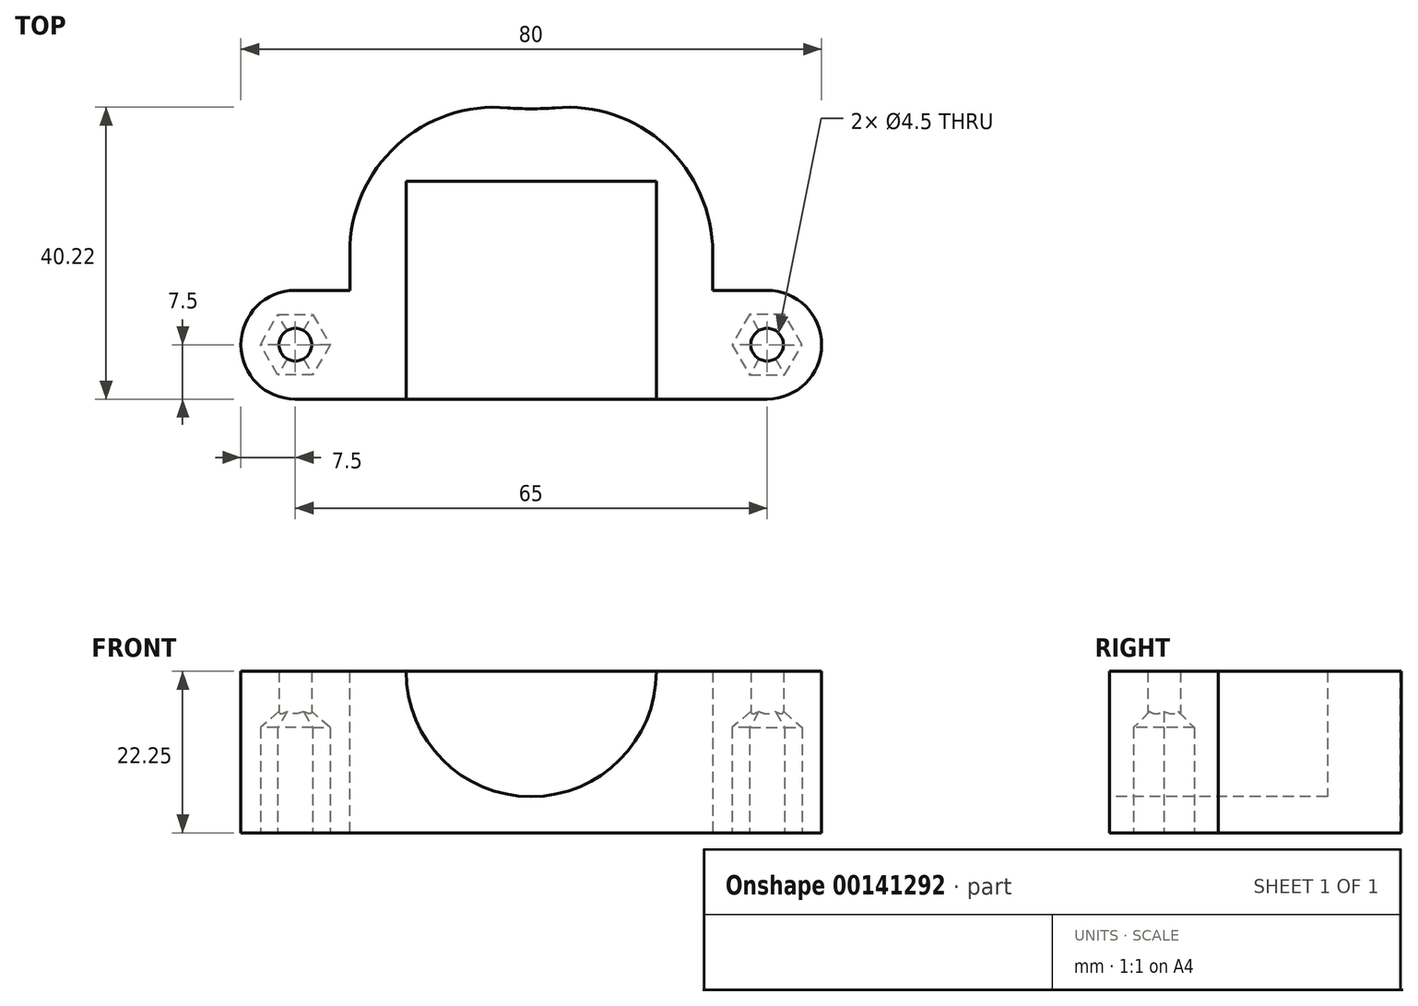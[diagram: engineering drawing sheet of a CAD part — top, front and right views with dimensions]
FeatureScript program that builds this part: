
annotation { "Feature Type Name" : "Feature", "Feature Type Description" : "" }
export const myFeature = defineFeature(function(context is Context, id is Id, definition is map)
    precondition{}
    {
        {
            var Q0;
            Q0=qCreatedBy(makeId("Top.planeOp"),FACE);
            var sketch = newSketch(context, id + "F0", { "sketchPlane" : qUnion([Q0])});
            skArc(sketch, "E0", {"start": v(38.1, 0) * mm, "mid": v(0, 38.1) * mm, "end": v(-38.1, 0) * mm});
            skCircle(sketch, "E1", {"center": v(0, 0) * mm, "radius": 5 * mm});
            skArc(sketch, "E2", {"start": v(-38.1, 0) * mm, "mid": v(0, -38.1) * mm, "end": v(38.1, 0) * mm});
            skSolve(sketch);
        }
        {
            var Q0;
            Q0=qSketchRegion(id+"F0",true);
            extrude(context, id + "F1", {"entities" : qUnion([Q0]), "depth" : 14 * mm});
        }
        {
            var Q0;
            Q0=makeQuery(id+"F1.opExtrude","CAP_FACE",FACE,{"disambiguationData":[OSD([sQuery(id+"F0.wireOp",EDGE,"E0"),sQuery(id+"F0.wireOp",EDGE,"E1"),sQuery(id+"F0.wireOp",EDGE,"E2")])],"isStart":false});
            var sketch = newSketch(context, id + "F2", { "sketchPlane" : qUnion([Q0])});
            skLineSegment(sketch, "E3.bottom", {"start": v(34.03, -2) * mm, "end": v(14.53, -2) * mm});
            skLineSegment(sketch, "E3.top", {"start": v(34.03, 2) * mm, "end": v(14.53, 2) * mm});
            skLineSegment(sketch, "E3.left", {"start": v(36.02, -2) * mm, "end": v(36.02, 2) * mm, "construction": true});
            skLineSegment(sketch, "E3.right", {"start": v(14.53, -2) * mm, "end": v(14.53, 2) * mm});
            skPoint(sketch, "E3.middle", {"position": v(25.28, 0) * mm});
            skArc(sketch, "E4", {"start": v(34.03, 2) * mm, "mid": v(36.03, 0) * mm, "end": v(34.03, -2) * mm});
            skSolve(sketch);
        }
        {
            var Q0;
            Q0=qSketchRegion(id+"F2",true);
            extrude(context, id + "F3", {"entities" : qUnion([Q0]), "operationType" : NewBodyOperationType.REMOVE, "oppositeDirection" : true, "depth" : 4 * mm});
        }
        {
            var Q0;
            Q0=makeQuery(id+"F3.boolean.opBoolean","COPY",EDGE,{"derivedFrom":makeQuery(id+"F3.opExtrude","CAP_EDGE",EDGE,{"disambiguationData":[OSD([sQuery(id+"F2.wireOp",EDGE,"E3.top")])],"isStart":false})});
            fillet(context, id + "F4", {"entities" : qUnion([Q0]), "radius" : 2 * mm, "tangentPropagation" : true, "allowEdgeOverflow" : false});
        }
        {
            var Q0;
            Q0=qCreatedBy(makeId("Top.planeOp"),FACE);
            var sketch = newSketch(context, id + "F5", { "sketchPlane" : qUnion([Q0])});
            skArc(sketch, "E5", {"start": v(-25, -28.75) * mm, "mid": v(-13.35, -35.69) * mm, "end": v(0, -38.1) * mm});
            skLineSegment(sketch, "E6", {"start": v(-25, -28.75) * mm, "end": v(-25, -63.1) * mm});
            skLineSegment(sketch, "E7", {"start": v(-25, -78.1) * mm, "end": v(0, -78.1) * mm});
            skArc(sketch, "E8.MirrorCS", {"start": v(25, -28.75) * mm, "mid": v(13.35, -35.69) * mm, "end": v(0, -38.1) * mm});
            skLineSegment(sketch, "E9.MirrorCS", {"start": v(25, -28.75) * mm, "end": v(25, -63.1) * mm});
            skLineSegment(sketch, "E10.MirrorCS", {"start": v(25, -78.1) * mm, "end": v(0, -78.1) * mm});
            skLineSegment(sketch, "E11", {"start": v(-25, -63.1) * mm, "end": v(-40, -63.1) * mm});
            skLineSegment(sketch, "E12", {"start": v(-40, -63.1) * mm, "end": v(-40, -78.1) * mm});
            skLineSegment(sketch, "E13", {"start": v(-40, -78.1) * mm, "end": v(-25, -78.1) * mm});
            skLineSegment(sketch, "E14.MirrorCS", {"start": v(25, -63.1) * mm, "end": v(40, -63.1) * mm});
            skLineSegment(sketch, "E15.MirrorCS", {"start": v(40, -63.1) * mm, "end": v(40, -78.1) * mm});
            skLineSegment(sketch, "E16.MirrorCS", {"start": v(40, -78.1) * mm, "end": v(25, -78.1) * mm});
            skPoint(sketch, "E17.orphan", {"position": v(25, -78.1) * mm});
            skCircle(sketch, "E18", {"center": v(-32.5, -70.6) * mm, "radius": 2.25 * mm});
            skCircle(sketch, "E19.MirrorC", {"center": v(32.5, -70.6) * mm, "radius": 2.25 * mm});
            skSolve(sketch);
        }
        {
            var Q0;
            Q0=qSketchRegion(id+"F5",true);
            extrude(context, id + "F6", {"entities" : qUnion([Q0]), "operationType" : NewBodyOperationType.ADD, "depth" : 22.25 * mm});
        }
        {
            var Q0;
            Q0=makeQuery(id+"F6.opExtrude","SWEPT_FACE",FACE,{"disambiguationData":[OSD([sQuery(id+"F5.wireOp",EDGE,"E7"),sQuery(id+"F5.wireOp",EDGE,"E10.MirrorCS")])]});
            var sketch = newSketch(context, id + "F7", { "sketchPlane" : qUnion([Q0])});
            skCircle(sketch, "E20", {"center": v(0, 22.25) * mm, "radius": 17.25 * mm});
            skSolve(sketch);
        }
        {
            var Q0;
            Q0=qSketchRegion(id+"F7",true);
            extrude(context, id + "F8", {"entities" : qUnion([Q0]), "operationType" : NewBodyOperationType.REMOVE, "oppositeDirection" : true, "depth" : 30 * mm});
        }
        {
            var Q0;
            Q0=qCreatedBy(makeId("Top.planeOp"),FACE);
            var sketch = newSketch(context, id + "F9", { "sketchPlane" : qUnion([Q0])});
            skCircle(sketch, "E21.cCircle", {"center": v(-32.5, -70.6) * mm, "radius": 4.17 * mm, "construction": true});
            skLineSegment(sketch, "E21.0", {"start": v(-34.91, -66.42) * mm, "end": v(-30.09, -66.42) * mm});
            skLineSegment(sketch, "E21.1", {"start": v(-30.09, -66.42) * mm, "end": v(-27.68, -70.6) * mm});
            skLineSegment(sketch, "E21.2", {"start": v(-27.68, -70.6) * mm, "end": v(-30.09, -74.77) * mm});
            skLineSegment(sketch, "E21.3", {"start": v(-30.09, -74.77) * mm, "end": v(-34.91, -74.77) * mm});
            skLineSegment(sketch, "E21.4", {"start": v(-34.91, -74.77) * mm, "end": v(-37.32, -70.6) * mm});
            skLineSegment(sketch, "E21.5", {"start": v(-37.32, -70.6) * mm, "end": v(-34.91, -66.42) * mm});
            skPoint(sketch, "E21.0.midPoint", {"position": v(-32.5, -66.42) * mm});
            skPoint(sketch, "E22.MirrorP", {"position": v(32.5, -66.42) * mm});
            skCircle(sketch, "E23.MirrorC", {"center": v(32.5, -70.6) * mm, "radius": 4.17 * mm, "construction": true});
            skLineSegment(sketch, "E24.MirrorCS", {"start": v(27.68, -70.6) * mm, "end": v(30.09, -74.77) * mm});
            skLineSegment(sketch, "E25.MirrorCS", {"start": v(30.09, -74.77) * mm, "end": v(34.91, -74.77) * mm});
            skLineSegment(sketch, "E26.MirrorCS", {"start": v(30.09, -66.42) * mm, "end": v(27.68, -70.6) * mm});
            skLineSegment(sketch, "E27.MirrorCS", {"start": v(34.91, -66.42) * mm, "end": v(30.09, -66.42) * mm});
            skLineSegment(sketch, "E28.MirrorCS", {"start": v(34.91, -74.77) * mm, "end": v(37.32, -70.6) * mm});
            skLineSegment(sketch, "E29.MirrorCS", {"start": v(37.32, -70.6) * mm, "end": v(34.91, -66.42) * mm});
            skSolve(sketch);
        }
        {
            var Q0;
            Q0=qSketchRegion(id+"F9",true);
            extrude(context, id + "F10", {"entities" : qUnion([Q0]), "operationType" : NewBodyOperationType.REMOVE, "depth" : 17 * mm});
        }
        {
            var Q0;
            Q0=makeQuery(id+"F10.boolean.opBoolean","COPY",EDGE,{"derivedFrom":makeQuery(id+"F10.opExtrude","CAP_EDGE",EDGE,{"disambiguationData":[OSD([sQuery(id+"F9.wireOp",EDGE,"E27.MirrorCS")])],"isStart":false})});
            var Q1;
            Q1=makeQuery(id+"F10.boolean.opBoolean","COPY",EDGE,{"derivedFrom":makeQuery(id+"F10.opExtrude","CAP_EDGE",EDGE,{"disambiguationData":[OSD([sQuery(id+"F9.wireOp",EDGE,"E26.MirrorCS")])],"isStart":false})});
            var Q2;
            Q2=makeQuery(id+"F10.boolean.opBoolean","COPY",EDGE,{"derivedFrom":makeQuery(id+"F10.opExtrude","CAP_EDGE",EDGE,{"disambiguationData":[OSD([sQuery(id+"F9.wireOp",EDGE,"E24.MirrorCS")])],"isStart":false})});
            var Q3;
            Q3=makeQuery(id+"F10.boolean.opBoolean","COPY",EDGE,{"derivedFrom":makeQuery(id+"F10.opExtrude","CAP_EDGE",EDGE,{"disambiguationData":[OSD([sQuery(id+"F9.wireOp",EDGE,"E25.MirrorCS")])],"isStart":false})});
            var Q4;
            Q4=makeQuery(id+"F10.boolean.opBoolean","COPY",EDGE,{"derivedFrom":makeQuery(id+"F10.opExtrude","CAP_EDGE",EDGE,{"disambiguationData":[OSD([sQuery(id+"F9.wireOp",EDGE,"E28.MirrorCS")])],"isStart":false})});
            var Q5;
            Q5=makeQuery(id+"F10.boolean.opBoolean","COPY",EDGE,{"derivedFrom":makeQuery(id+"F10.opExtrude","CAP_EDGE",EDGE,{"disambiguationData":[OSD([sQuery(id+"F9.wireOp",EDGE,"E29.MirrorCS")])],"isStart":false})});
            var Q6;
            Q6=makeQuery(id+"F10.boolean.opBoolean","COPY",EDGE,{"derivedFrom":makeQuery(id+"F10.opExtrude","CAP_EDGE",EDGE,{"disambiguationData":[OSD([sQuery(id+"F9.wireOp",EDGE,"E21.1")])],"isStart":false})});
            var Q7;
            Q7=makeQuery(id+"F10.boolean.opBoolean","COPY",EDGE,{"derivedFrom":makeQuery(id+"F10.opExtrude","CAP_EDGE",EDGE,{"disambiguationData":[OSD([sQuery(id+"F9.wireOp",EDGE,"E21.0")])],"isStart":false})});
            var Q8;
            Q8=makeQuery(id+"F10.boolean.opBoolean","COPY",EDGE,{"derivedFrom":makeQuery(id+"F10.opExtrude","CAP_EDGE",EDGE,{"disambiguationData":[OSD([sQuery(id+"F9.wireOp",EDGE,"E21.5")])],"isStart":false})});
            var Q9;
            Q9=makeQuery(id+"F10.boolean.opBoolean","COPY",EDGE,{"derivedFrom":makeQuery(id+"F10.opExtrude","CAP_EDGE",EDGE,{"disambiguationData":[OSD([sQuery(id+"F9.wireOp",EDGE,"E21.4")])],"isStart":false})});
            var Q10;
            Q10=makeQuery(id+"F10.boolean.opBoolean","COPY",EDGE,{"derivedFrom":makeQuery(id+"F10.opExtrude","CAP_EDGE",EDGE,{"disambiguationData":[OSD([sQuery(id+"F9.wireOp",EDGE,"E21.3")])],"isStart":false})});
            var Q11;
            Q11=makeQuery(id+"F10.boolean.opBoolean","COPY",EDGE,{"derivedFrom":makeQuery(id+"F10.opExtrude","CAP_EDGE",EDGE,{"disambiguationData":[OSD([sQuery(id+"F9.wireOp",EDGE,"E21.2")])],"isStart":false})});
            chamfer(context, id + "F11", {"entities" : qUnion([Q0, Q1, Q2, Q3, Q4, Q5, Q6, Q7, Q8, Q9, Q10, Q11]), "width" : 2.5 * mm, "tangentPropagation" : true});
        }
        {
            var Q0;
            {var subQ0=sQuery(id+"F5.wireOp",EDGE,"E5");var subQ1=sQuery(id+"F5.wireOp",EDGE,"E6");Q0=makeQuery(id+"F6.boolean.opBoolean","SPLIT",EDGE,{"disambiguationData":[topologyDisambiguationEdgeConnected([makeQuery(id+"F6.opExtrude","SWEPT_FACE",FACE,{"disambiguationData":[OSD([subQ0,sQuery(id+"F5.wireOp",EDGE,"E8.MirrorCS")])]})])],"derivedFrom":makeQuery(id+"F6.opExtrude","SWEPT_EDGE",EDGE,{"disambiguationData":[OSD([subQ0,subQ1])]})});}
            var Q1;
            {var subQ0=sQuery(id+"F5.wireOp",EDGE,"E8.MirrorCS");var subQ1=sQuery(id+"F5.wireOp",EDGE,"E9.MirrorCS");Q1=makeQuery(id+"F6.boolean.opBoolean","SPLIT",EDGE,{"disambiguationData":[topologyDisambiguationEdgeConnected([makeQuery(id+"F6.opExtrude","SWEPT_FACE",FACE,{"disambiguationData":[OSD([sQuery(id+"F5.wireOp",EDGE,"E5"),subQ0])]})])],"derivedFrom":makeQuery(id+"F6.opExtrude","SWEPT_EDGE",EDGE,{"disambiguationData":[OSD([subQ0,subQ1])]})});}
            fillet(context, id + "F12", {"entities" : qUnion([Q0, Q1]), "radius" : 20 * mm, "tangentPropagation" : true, "allowEdgeOverflow" : false});
        }
        {
            var Q0;
            Q0=makeQuery(id+"F6.opExtrude","SWEPT_EDGE",EDGE,{"disambiguationData":[OSD([sQuery(id+"F5.wireOp",EDGE,"E11"),sQuery(id+"F5.wireOp",EDGE,"E12")])]});
            var Q1;
            Q1=makeQuery(id+"F6.opExtrude","SWEPT_EDGE",EDGE,{"disambiguationData":[OSD([sQuery(id+"F5.wireOp",EDGE,"E12"),sQuery(id+"F5.wireOp",EDGE,"E13")])]});
            var Q2;
            Q2=makeQuery(id+"F6.opExtrude","SWEPT_EDGE",EDGE,{"disambiguationData":[OSD([sQuery(id+"F5.wireOp",EDGE,"E15.MirrorCS"),sQuery(id+"F5.wireOp",EDGE,"E16.MirrorCS")])]});
            var Q3;
            Q3=makeQuery(id+"F6.opExtrude","SWEPT_EDGE",EDGE,{"disambiguationData":[OSD([sQuery(id+"F5.wireOp",EDGE,"E14.MirrorCS"),sQuery(id+"F5.wireOp",EDGE,"E15.MirrorCS")])]});
            fillet(context, id + "F13", {"entities" : qUnion([Q0, Q1, Q2, Q3]), "radius" : 7.5 * mm, "tangentPropagation" : true, "allowEdgeOverflow" : false});
        }
        {
            var Q0;
            Q0=makeQuery(id+"F1.opExtrude","CAP_FACE",FACE,{"disambiguationData":[OSD([sQuery(id+"F0.wireOp",EDGE,"E0"),sQuery(id+"F0.wireOp",EDGE,"E1"),sQuery(id+"F0.wireOp",EDGE,"E2")])],"isStart":false});
            var sketch = newSketch(context, id + "F14", { "sketchPlane" : qUnion([Q0])});
            skArc(sketch, "E30", {"start": v(25, -28.75) * mm, "mid": v(0, 38.1) * mm, "end": v(-25, -28.75) * mm});
            skLineSegment(sketch, "E31", {"start": v(-25, -57.88) * mm, "end": v(-25, -28.75) * mm});
            skLineSegment(sketch, "E32", {"start": v(25, -57.88) * mm, "end": v(25, -28.75) * mm});
            skArc(sketch, "E33", {"start": v(-3.28, -37.96) * mm, "mid": v(0, -38.1) * mm, "end": v(3.28, -37.96) * mm});
            skArc(sketch, "E34", {"start": v(25, -57.88) * mm, "mid": v(18.52, -43.15) * mm, "end": v(3.28, -37.96) * mm});
            skArc(sketch, "E35", {"start": v(-3.28, -37.96) * mm, "mid": v(-18.52, -43.15) * mm, "end": v(-25, -57.88) * mm});
            skSolve(sketch);
        }
        {
            var Q0;
            Q0 = qSketchRegion(id + "F14", true);
            extrude(context, id + "F15", {"entities" : qUnion([Q0]), "operationType" : NewBodyOperationType.REMOVE, "endBound" : BoundingType.THROUGH_ALL, "oppositeDirection" : true, "depth" : 25 * mm});
        }
    });
